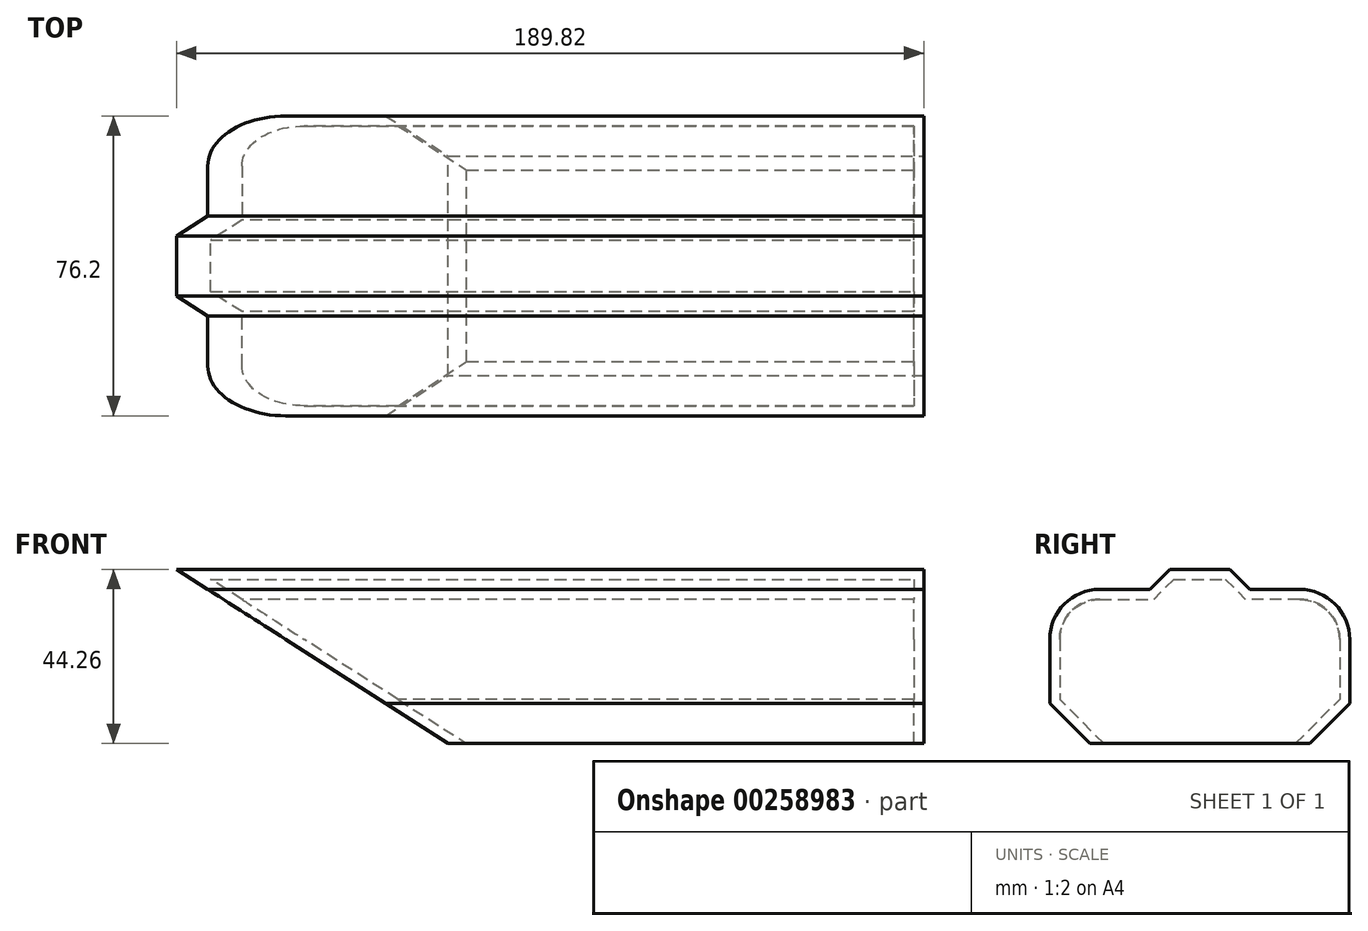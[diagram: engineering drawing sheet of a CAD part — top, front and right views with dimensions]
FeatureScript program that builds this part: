
annotation { "Feature Type Name" : "Feature", "Feature Type Description" : "" }
export const myFeature = defineFeature(function(context is Context, id is Id, definition is map)
    precondition{}
    {
        {
            var Q0;
            Q0=qCreatedBy(makeId("Front.planeOp"),FACE);
            var sketch = newSketch(context, id + "F0", { "sketchPlane" : qUnion([Q0])});
            skLineSegment(sketch, "E0", {"start": v(65.97, 12.24) * mm, "end": v(-123.85, 12.24) * mm});
            skLineSegment(sketch, "E1", {"start": v(65.97, 12.24) * mm, "end": v(65.97, -32.02) * mm});
            skLineSegment(sketch, "E2", {"start": v(65.97, -32.02) * mm, "end": v(-54.85, -32.02) * mm});
            skLineSegment(sketch, "E3", {"start": v(-54.85, -32.02) * mm, "end": v(-123.85, 12.24) * mm});
            skSolve(sketch);
        }
        {
            var Q0;
            Q0=makeQuery(id+"F0.imprint","IMPRINT",FACE,{"disambiguationData":[TD([[makeQuery(id+"F0.imprint","IMPRINT",EDGE,{"derivedFrom":sQuery(id+"F0.wireOp",EDGE,"E0")}),1.0]])]});
            var Q1;
            Q1 = qSketchRegion(id + "F0", true);
            extrude(context, id + "F1", {"entities" : qUnion([Q0, Q1]), "depth" : 25.4 * mm});
        }
        {
            var Q0;
            Q0=makeQuery(id+"F1.opExtrude","CAP_EDGE",EDGE,{"disambiguationData":[OSD([sQuery(id+"F0.wireOp",EDGE,"E0")])],"isStart":false});
            chamfer(context, id + "F2", {"entities" : qUnion([Q0]), "width" : 5.08 * mm, "tangentPropagation" : true});
        }
        {
            var Q0;
            Q0=makeQuery(id+"F1.opExtrude","CAP_EDGE",EDGE,{"disambiguationData":[OSD([sQuery(id+"F0.wireOp",EDGE,"E0")])],"isStart":true});
            chamfer(context, id + "F3", {"entities" : qUnion([Q0]), "width" : 5.08 * mm, "tangentPropagation" : true});
        }
        {
            var Q0;
            Q0=makeQuery(id+"F1.opExtrude","CAP_FACE",FACE,{"disambiguationData":[OSD([sQuery(id+"F0.wireOp",EDGE,"E0"),sQuery(id+"F0.wireOp",EDGE,"E1"),sQuery(id+"F0.wireOp",EDGE,"E2"),sQuery(id+"F0.wireOp",EDGE,"E3")])],"isStart":true});
            extrude(context, id + "F4", {"entities" : qUnion([Q0]), "operationType" : NewBodyOperationType.ADD, "depth" : 25.4 * mm});
        }
        {
            var Q0;
            Q0=makeQuery(id+"F1.opExtrude","CAP_FACE",FACE,{"disambiguationData":[OSD([sQuery(id+"F0.wireOp",EDGE,"E0"),sQuery(id+"F0.wireOp",EDGE,"E1"),sQuery(id+"F0.wireOp",EDGE,"E2"),sQuery(id+"F0.wireOp",EDGE,"E3")])],"isStart":false});
            extrude(context, id + "F5", {"entities" : qUnion([Q0]), "operationType" : NewBodyOperationType.ADD, "depth" : 25.4 * mm});
        }
        {
            var Q0;
            Q0=makeQuery(id+"F4.opExtrude","CAP_EDGE",EDGE,{"disambiguationData":[OSD([sQuery(id+"F0.wireOp",EDGE,"E2")])],"isStart":false});
            chamfer(context, id + "F6", {"entities" : qUnion([Q0]), "width" : 10.16 * mm, "tangentPropagation" : true});
        }
        {
            var Q0;
            Q0=makeQuery(id+"F5.opExtrude","CAP_EDGE",EDGE,{"disambiguationData":[OSD([sQuery(id+"F0.wireOp",EDGE,"E2")])],"isStart":false});
            chamfer(context, id + "F7", {"entities" : qUnion([Q0]), "width" : 10.16 * mm, "tangentPropagation" : true});
        }
        {
            var Q0;
            Q0=makeQuery(id+"F4.opExtrude","CAP_EDGE",EDGE,{"disambiguationData":[OSD([sQuery(id+"F0.wireOp",EDGE,"E0"),sQuery(id+"F0.wireOp",EDGE,"E1"),sQuery(id+"F0.wireOp",EDGE,"E2"),sQuery(id+"F0.wireOp",EDGE,"E3")])],"isStart":false});
            fillet(context, id + "F8", {"entities" : qUnion([Q0]), "radius" : 12.7 * mm, "tangentPropagation" : true, "allowEdgeOverflow" : false});
        }
        {
            var Q0;
            Q0=makeQuery(id+"F5.opExtrude","CAP_EDGE",EDGE,{"disambiguationData":[OSD([sQuery(id+"F0.wireOp",EDGE,"E0"),sQuery(id+"F0.wireOp",EDGE,"E1"),sQuery(id+"F0.wireOp",EDGE,"E2"),sQuery(id+"F0.wireOp",EDGE,"E3")])],"isStart":false});
            fillet(context, id + "F9", {"entities" : qUnion([Q0]), "radius" : 12.7 * mm, "tangentPropagation" : true, "allowEdgeOverflow" : false});
        }
        {
            var Q0;
            {var subQ0=sQuery(id+"F0.wireOp",EDGE,"E2");Q0=makeQuery(id+"F5.boolean.opBoolean","MERGE",FACE,{"derivedFrom":[makeQuery(id+"F4.boolean.opBoolean","MERGE",FACE,{"derivedFrom":[makeQuery(id+"F1.opExtrude","SWEPT_FACE",FACE,{"disambiguationData":[OSD([subQ0])]}),makeQuery(id+"F4.opExtrude","SWEPT_FACE",FACE,{"disambiguationData":[OSD([subQ0])]})]}),makeQuery(id+"F5.opExtrude","SWEPT_FACE",FACE,{"disambiguationData":[OSD([subQ0])]})]});}
            shell(context, id + "F10", {"entities" : qUnion([Q0]), "thickness" : 2.54 * mm});
        }
    });
